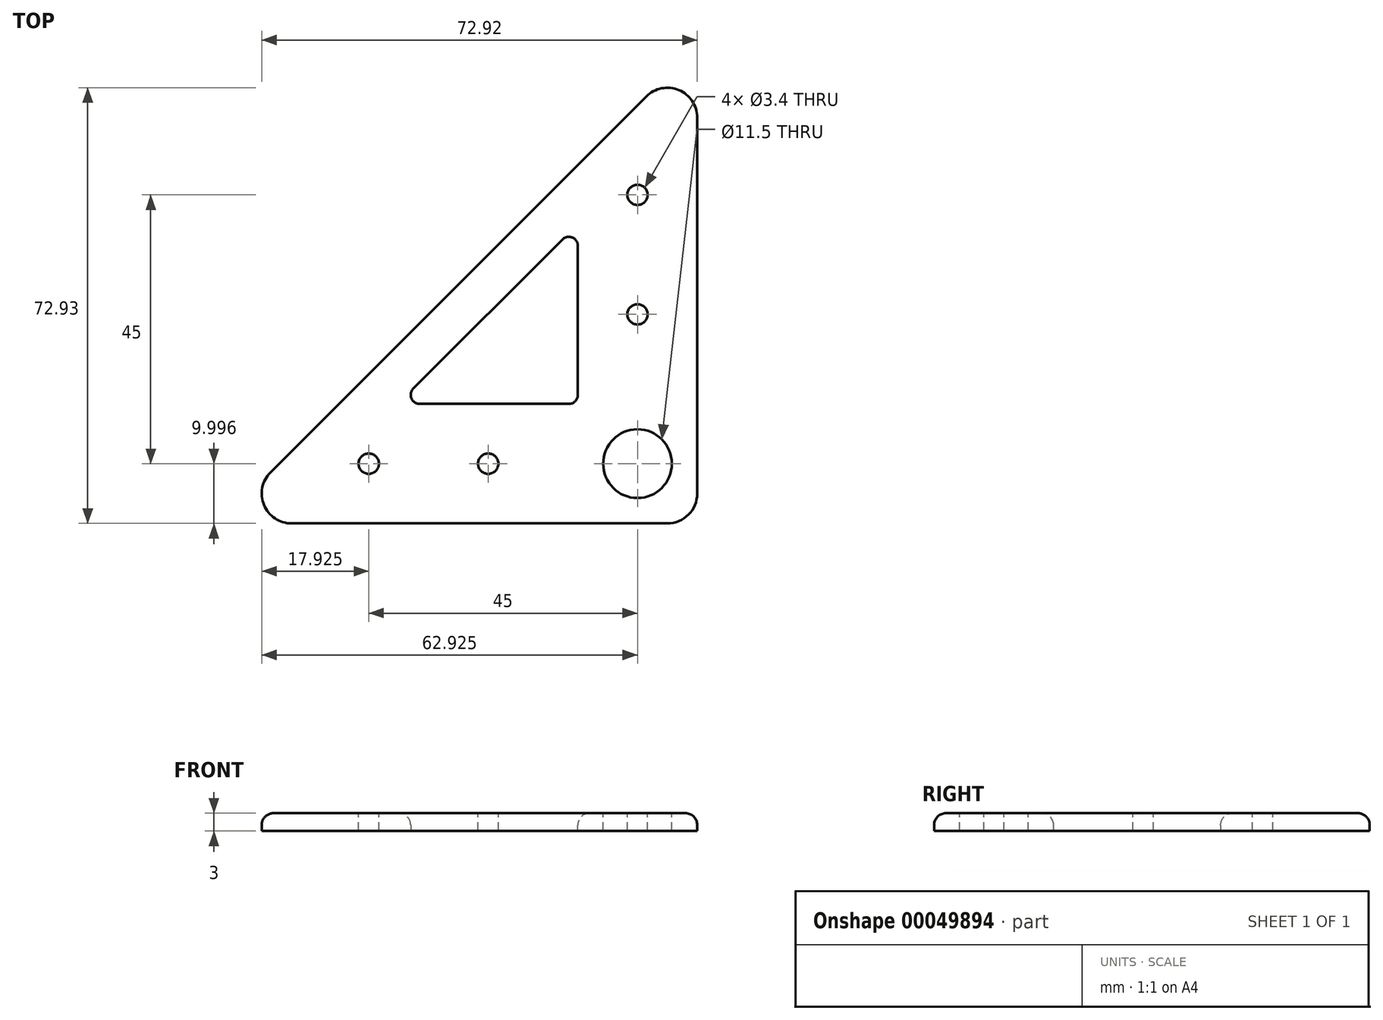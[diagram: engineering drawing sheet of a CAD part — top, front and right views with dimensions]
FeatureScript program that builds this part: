
annotation { "Feature Type Name" : "Feature", "Feature Type Description" : "" }
export const myFeature = defineFeature(function(context is Context, id is Id, definition is map)
    precondition{}
    {
        {
            var Q0;
            Q0=qCreatedBy(makeId("Top.planeOp"),FACE);
            var sketch = newSketch(context, id + "F0", { "sketchPlane" : qUnion([Q0])});
            skLineSegment(sketch, "E0", {"start": v(-29.17, -20.35) * mm, "end": v(50.83, -20.35) * mm});
            skLineSegment(sketch, "E1", {"start": v(50.83, -20.35) * mm, "end": v(50.83, 59.65) * mm});
            skLineSegment(sketch, "E2", {"start": v(50.83, 59.65) * mm, "end": v(-29.17, -20.35) * mm});
            skSolve(sketch);
        }
        {
            var Q0;
            Q0=makeQuery(id+"F0.imprint","IMPRINT",FACE,{"disambiguationData":[TD([[makeQuery(id+"F0.imprint","IMPRINT",EDGE,{"derivedFrom":sQuery(id+"F0.wireOp",EDGE,"E0")}),1.0]])]});
            extrude(context, id + "F1", {"entities" : qUnion([Q0]), "depth" : 3 * mm});
        }
        {
            var Q0;
            Q0=makeQuery(id+"F1.opExtrude","CAP_FACE",FACE,{"disambiguationData":[OSD([sQuery(id+"F0.wireOp",EDGE,"E0"),sQuery(id+"F0.wireOp",EDGE,"E1"),sQuery(id+"F0.wireOp",EDGE,"E2")])],"isStart":false});
            var sketch = newSketch(context, id + "F2", { "sketchPlane" : qUnion([Q0])});
            skLineSegment(sketch, "E3", {"start": v(30.83, -0.35) * mm, "end": v(0.73, -0.35) * mm});
            skLineSegment(sketch, "E4", {"start": v(30.83, 29.75) * mm, "end": v(30.83, -0.35) * mm});
            skLineSegment(sketch, "E5", {"start": v(0.73, -0.35) * mm, "end": v(30.83, 29.75) * mm});
            skCircle(sketch, "E6", {"center": v(40.83, -10.35) * mm, "radius": 5.75 * mm});
            skCircle(sketch, "E7", {"center": v(15.83, -10.35) * mm, "radius": 1.7 * mm});
            skCircle(sketch, "E8", {"center": v(-4.17, -10.35) * mm, "radius": 1.7 * mm});
            skCircle(sketch, "E9", {"center": v(40.83, 14.65) * mm, "radius": 1.7 * mm});
            skCircle(sketch, "E10", {"center": v(40.83, 34.65) * mm, "radius": 1.7 * mm});
            skSolve(sketch);
        }
        {
            var Q0;
            Q0 = qSketchRegion(id + "F2", true);
            var Q1;
            Q1=makeQuery(id+"F1.opExtrude","CAP_FACE",FACE,{"disambiguationData":[OSD([sQuery(id+"F0.wireOp",EDGE,"E0"),sQuery(id+"F0.wireOp",EDGE,"E1"),sQuery(id+"F0.wireOp",EDGE,"E2")])],"isStart":true});
            extrude(context, id + "F3", {"entities" : qUnion([Q0]), "operationType" : NewBodyOperationType.REMOVE, "endBound" : BoundingType.UP_TO_SURFACE, "oppositeDirection" : true, "endBoundEntityFace" : qUnion([Q1]), "depth" : 25 * mm});
        }
        {
            var Q0;
            Q0=makeQuery(id+"F3.boolean.opBoolean","COPY",EDGE,{"derivedFrom":makeQuery(id+"F3.opExtrude","SWEPT_EDGE",EDGE,{"disambiguationData":[OSD([sQuery(id+"F2.wireOp",EDGE,"E3"),sQuery(id+"F2.wireOp",EDGE,"E5")])]})});
            var Q1;
            Q1=makeQuery(id+"F3.boolean.opBoolean","COPY",EDGE,{"derivedFrom":makeQuery(id+"F3.opExtrude","SWEPT_EDGE",EDGE,{"disambiguationData":[OSD([sQuery(id+"F2.wireOp",EDGE,"E3"),sQuery(id+"F2.wireOp",EDGE,"E4")])]})});
            var Q2;
            Q2=makeQuery(id+"F3.boolean.opBoolean","COPY",EDGE,{"derivedFrom":makeQuery(id+"F3.opExtrude","SWEPT_EDGE",EDGE,{"disambiguationData":[OSD([sQuery(id+"F2.wireOp",EDGE,"E4"),sQuery(id+"F2.wireOp",EDGE,"E5")])]})});
            fillet(context, id + "F4", {"entities" : qUnion([Q0, Q1, Q2]), "radius" : 1.5 * mm, "tangentPropagation" : true, "allowEdgeOverflow" : false});
        }
        {
            var Q0;
            Q0=makeQuery(id+"F1.opExtrude","SWEPT_EDGE",EDGE,{"disambiguationData":[OSD([sQuery(id+"F0.wireOp",EDGE,"E0"),sQuery(id+"F0.wireOp",EDGE,"E2")])]});
            var Q1;
            Q1=makeQuery(id+"F1.opExtrude","SWEPT_EDGE",EDGE,{"disambiguationData":[OSD([sQuery(id+"F0.wireOp",EDGE,"E0"),sQuery(id+"F0.wireOp",EDGE,"E1")])]});
            var Q2;
            Q2=makeQuery(id+"F1.opExtrude","SWEPT_EDGE",EDGE,{"disambiguationData":[OSD([sQuery(id+"F0.wireOp",EDGE,"E1"),sQuery(id+"F0.wireOp",EDGE,"E2")])]});
            fillet(context, id + "F5", {"entities" : qUnion([Q0, Q1, Q2]), "radius" : 5 * mm, "tangentPropagation" : true, "allowEdgeOverflow" : false});
        }
        {
            var Q0;
            Q0=makeQuery(id+"F1.opExtrude","CAP_EDGE",EDGE,{"disambiguationData":[OSD([sQuery(id+"F0.wireOp",EDGE,"E0")])],"isStart":false});
            var Q1;
            {var subQ0=sQuery(id+"F0.wireOp",EDGE,"E1");var subQ1=sQuery(id+"F0.wireOp",EDGE,"E0");Q1=makeQuery(id+"F5.opFillet","BLEND_EDGE",EDGE,{"blendedFrom":[makeQuery(id+"F1.opExtrude","SWEPT_EDGE",EDGE,{"disambiguationData":[OSD([subQ1,subQ0])]}),makeQuery(id+"F1.opExtrude","CAP_FACE",FACE,{"disambiguationData":[OSD([subQ1,subQ0,sQuery(id+"F0.wireOp",EDGE,"E2")])],"isStart":false})],"blendedInto":[makeQuery(id+"F1.opExtrude","CAP_FACE",FACE,{"disambiguationData":[OSD([subQ1,subQ0,sQuery(id+"F0.wireOp",EDGE,"E2")])],"isStart":false})]});}
            var Q2;
            Q2=makeQuery(id+"F1.opExtrude","CAP_EDGE",EDGE,{"disambiguationData":[OSD([sQuery(id+"F0.wireOp",EDGE,"E1")])],"isStart":false});
            var Q3;
            {var subQ0=sQuery(id+"F0.wireOp",EDGE,"E2");var subQ1=sQuery(id+"F0.wireOp",EDGE,"E0");Q3=makeQuery(id+"F5.opFillet","BLEND_EDGE",EDGE,{"blendedFrom":[makeQuery(id+"F1.opExtrude","SWEPT_EDGE",EDGE,{"disambiguationData":[OSD([subQ1,subQ0])]}),makeQuery(id+"F1.opExtrude","CAP_FACE",FACE,{"disambiguationData":[OSD([subQ1,sQuery(id+"F0.wireOp",EDGE,"E1"),subQ0])],"isStart":false})],"blendedInto":[makeQuery(id+"F1.opExtrude","CAP_FACE",FACE,{"disambiguationData":[OSD([subQ1,sQuery(id+"F0.wireOp",EDGE,"E1"),subQ0])],"isStart":false})]});}
            var Q4;
            Q4=makeQuery(id+"F1.opExtrude","CAP_EDGE",EDGE,{"disambiguationData":[OSD([sQuery(id+"F0.wireOp",EDGE,"E2")])],"isStart":false});
            var Q5;
            {var subQ0=sQuery(id+"F0.wireOp",EDGE,"E2");var subQ1=sQuery(id+"F0.wireOp",EDGE,"E1");Q5=makeQuery(id+"F5.opFillet","BLEND_EDGE",EDGE,{"blendedFrom":[makeQuery(id+"F1.opExtrude","SWEPT_EDGE",EDGE,{"disambiguationData":[OSD([subQ1,subQ0])]}),makeQuery(id+"F1.opExtrude","CAP_FACE",FACE,{"disambiguationData":[OSD([sQuery(id+"F0.wireOp",EDGE,"E0"),subQ1,subQ0])],"isStart":false})],"blendedInto":[makeQuery(id+"F1.opExtrude","CAP_FACE",FACE,{"disambiguationData":[OSD([sQuery(id+"F0.wireOp",EDGE,"E0"),subQ1,subQ0])],"isStart":false})]});}
            fillet(context, id + "F6", {"entities" : qUnion([Q0, Q1, Q2, Q3, Q4, Q5]), "radius" : 2 * mm, "tangentPropagation" : true, "allowEdgeOverflow" : false});
        }
        {
            var Q0;
            Q0=makeQuery(id+"F3.boolean.opBoolean","COPY",EDGE,{"derivedFrom":makeQuery(id+"F3.opExtrude","CAP_EDGE",EDGE,{"disambiguationData":[OSD([sQuery(id+"F2.wireOp",EDGE,"E3")])],"isStart":true})});
            var Q1;
            Q1=makeQuery(id+"F3.boolean.opBoolean","COPY",EDGE,{"derivedFrom":makeQuery(id+"F3.opExtrude","CAP_EDGE",EDGE,{"disambiguationData":[OSD([sQuery(id+"F2.wireOp",EDGE,"E4")])],"isStart":true})});
            var Q2;
            Q2=makeQuery(id+"F3.boolean.opBoolean","COPY",EDGE,{"derivedFrom":makeQuery(id+"F3.opExtrude","CAP_EDGE",EDGE,{"disambiguationData":[OSD([sQuery(id+"F2.wireOp",EDGE,"E5")])],"isStart":true})});
            var Q3;
            Q3=makeQuery(id+"F4.opFillet","BLEND_EDGE",EDGE,{"blendedFrom":[makeQuery(id+"F3.boolean.opBoolean","COPY",EDGE,{"derivedFrom":makeQuery(id+"F3.opExtrude","SWEPT_EDGE",EDGE,{"disambiguationData":[OSD([sQuery(id+"F2.wireOp",EDGE,"E3"),sQuery(id+"F2.wireOp",EDGE,"E4")])]})}),makeQuery(id+"F1.opExtrude","CAP_FACE",FACE,{"disambiguationData":[OSD([sQuery(id+"F0.wireOp",EDGE,"E0"),sQuery(id+"F0.wireOp",EDGE,"E1"),sQuery(id+"F0.wireOp",EDGE,"E2")])],"isStart":false})],"blendedInto":[makeQuery(id+"F1.opExtrude","CAP_FACE",FACE,{"disambiguationData":[OSD([sQuery(id+"F0.wireOp",EDGE,"E0"),sQuery(id+"F0.wireOp",EDGE,"E1"),sQuery(id+"F0.wireOp",EDGE,"E2")])],"isStart":false})]});
            var Q4;
            Q4=makeQuery(id+"F4.opFillet","BLEND_EDGE",EDGE,{"blendedFrom":[makeQuery(id+"F3.boolean.opBoolean","COPY",EDGE,{"derivedFrom":makeQuery(id+"F3.opExtrude","SWEPT_EDGE",EDGE,{"disambiguationData":[OSD([sQuery(id+"F2.wireOp",EDGE,"E3"),sQuery(id+"F2.wireOp",EDGE,"E5")])]})}),makeQuery(id+"F1.opExtrude","CAP_FACE",FACE,{"disambiguationData":[OSD([sQuery(id+"F0.wireOp",EDGE,"E0"),sQuery(id+"F0.wireOp",EDGE,"E1"),sQuery(id+"F0.wireOp",EDGE,"E2")])],"isStart":false})],"blendedInto":[makeQuery(id+"F1.opExtrude","CAP_FACE",FACE,{"disambiguationData":[OSD([sQuery(id+"F0.wireOp",EDGE,"E0"),sQuery(id+"F0.wireOp",EDGE,"E1"),sQuery(id+"F0.wireOp",EDGE,"E2")])],"isStart":false})]});
            var Q5;
            Q5=makeQuery(id+"F4.opFillet","BLEND_EDGE",EDGE,{"blendedFrom":[makeQuery(id+"F3.boolean.opBoolean","COPY",EDGE,{"derivedFrom":makeQuery(id+"F3.opExtrude","SWEPT_EDGE",EDGE,{"disambiguationData":[OSD([sQuery(id+"F2.wireOp",EDGE,"E4"),sQuery(id+"F2.wireOp",EDGE,"E5")])]})}),makeQuery(id+"F1.opExtrude","CAP_FACE",FACE,{"disambiguationData":[OSD([sQuery(id+"F0.wireOp",EDGE,"E0"),sQuery(id+"F0.wireOp",EDGE,"E1"),sQuery(id+"F0.wireOp",EDGE,"E2")])],"isStart":false})],"blendedInto":[makeQuery(id+"F1.opExtrude","CAP_FACE",FACE,{"disambiguationData":[OSD([sQuery(id+"F0.wireOp",EDGE,"E0"),sQuery(id+"F0.wireOp",EDGE,"E1"),sQuery(id+"F0.wireOp",EDGE,"E2")])],"isStart":false})]});
            fillet(context, id + "F7", {"entities" : qUnion([Q0, Q1, Q2, Q3, Q4, Q5]), "radius" : 2 * mm, "tangentPropagation" : true, "allowEdgeOverflow" : false});
        }
    });
